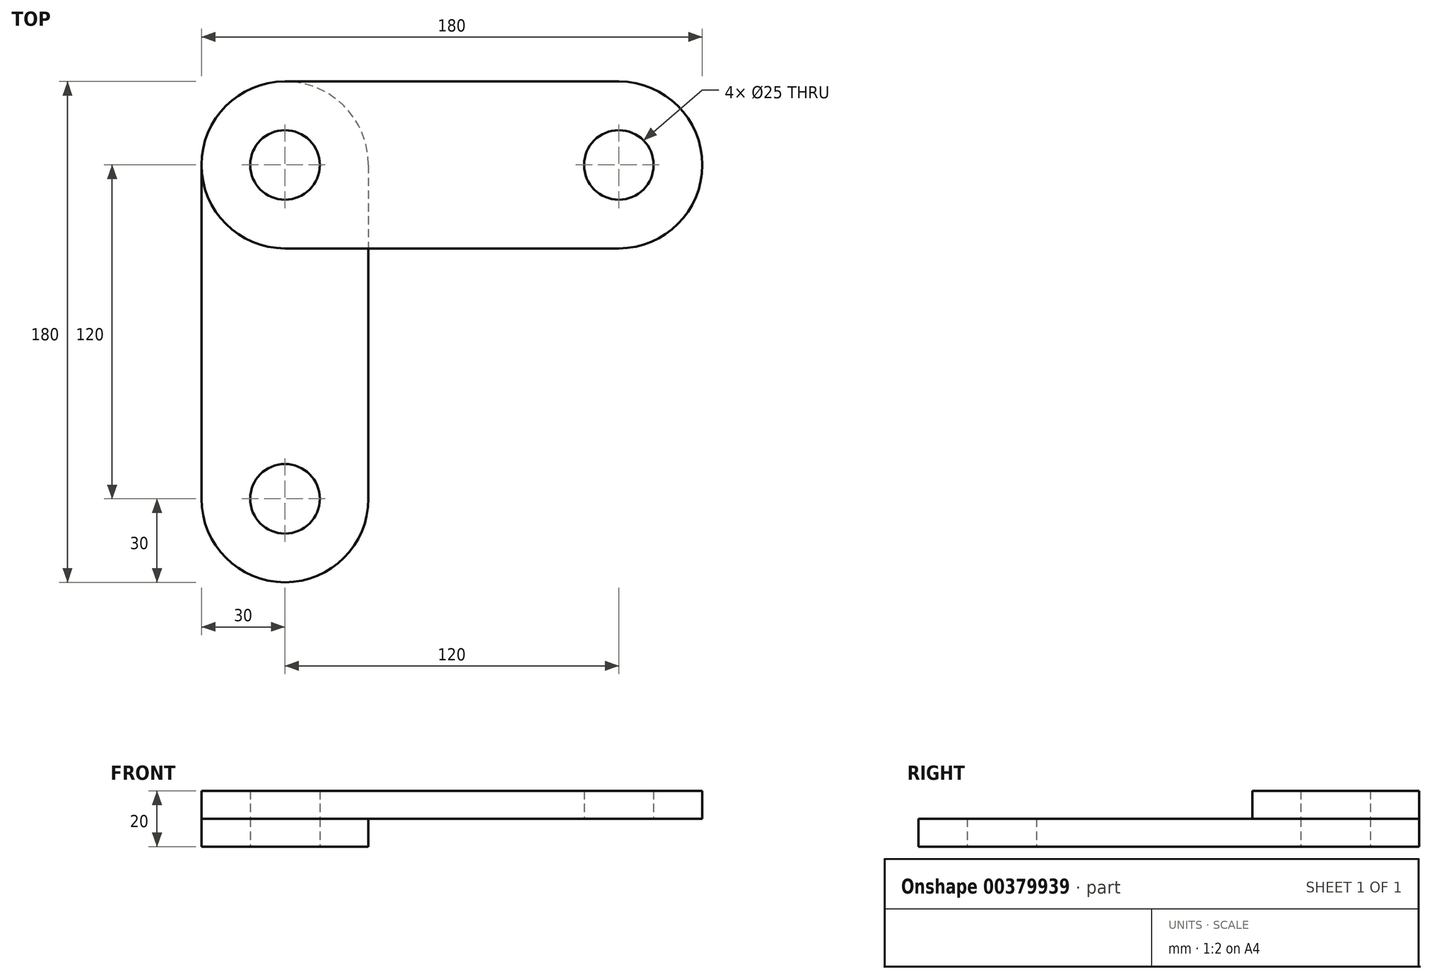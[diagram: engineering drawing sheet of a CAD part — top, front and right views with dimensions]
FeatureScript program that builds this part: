
annotation { "Feature Type Name" : "Feature", "Feature Type Description" : "" }
export const myFeature = defineFeature(function(context is Context, id is Id, definition is map)
    precondition{}
    {
        {
            var Q0;
            Q0=qCreatedBy(makeId("Top.planeOp"),FACE);
            var sketch = newSketch(context, id + "F0", { "sketchPlane" : qUnion([Q0])});
            skCircle(sketch, "E0", {"center": v(0, 0) * mm, "radius": 12.5 * mm});
            skCircle(sketch, "E1", {"center": v(0, 120) * mm, "radius": 12.5 * mm});
            skCircle(sketch, "E2", {"center": v(0, 120) * mm, "radius": 30 * mm});
            skCircle(sketch, "E3", {"center": v(0, 0) * mm, "radius": 30 * mm});
            skLineSegment(sketch, "E4", {"start": v(-30, 0) * mm, "end": v(-30, 120) * mm});
            skLineSegment(sketch, "E5", {"start": v(30, 120) * mm, "end": v(30, 0) * mm});
            skLineSegment(sketch, "E6", {"start": v(0, 120) * mm, "end": v(0, 0) * mm});
            skLineSegment(sketch, "E7", {"start": v(0, 0) * mm, "end": v(-30, 0) * mm, "construction": true});
            skLineSegment(sketch, "E8", {"start": v(0, 120) * mm, "end": v(-30, 120) * mm, "construction": true});
            skSolve(sketch);
        }
        {
            var Q0;
            {var subQ0=sQuery(id+"F0.wireOp",EDGE,"E4");Q0=makeQuery(id+"F0.imprint","IMPRINT",FACE,{"disambiguationData":[TD([[makeQuery(id+"F0.imprint","IMPRINT",EDGE,{"derivedFrom":subQ0}),-1.0]])]});}
            var Q1;
            {var subQ0=sQuery(id+"F0.wireOp",EDGE,"E5");Q1=makeQuery(id+"F0.imprint","IMPRINT",FACE,{"disambiguationData":[TD([[makeQuery(id+"F0.imprint","IMPRINT",EDGE,{"derivedFrom":subQ0}),-1.0]])]});}
            var Q2;
            Q2=makeQuery(id+"F0.imprint","IMPRINT",FACE,{"disambiguationData":[TD([[makeQuery(id+"F0.imprint","IMPRINT",EDGE,{"derivedFrom":sQuery(id+"F0.wireOp",EDGE,"E1")}),-1.0]])]});
            var Q3;
            Q3=makeQuery(id+"F0.imprint","IMPRINT",FACE,{"disambiguationData":[TD([[makeQuery(id+"F0.imprint","IMPRINT",EDGE,{"derivedFrom":sQuery(id+"F0.wireOp",EDGE,"E0")}),-1.0]])]});
            extrude(context, id + "F1", {"entities" : qUnion([Q0, Q1, Q2, Q3]), "depth" : 10 * mm});
        }
        {
            var Q0;
            Q0=makeQuery(id+"F1.opExtrude","SWEPT_BODY",BODY,{"disambiguationData":[OSD([sQuery(id+"F0.wireOp",EDGE,"E0"),sQuery(id+"F0.wireOp",EDGE,"E1"),sQuery(id+"F0.wireOp",EDGE,"E2"),sQuery(id+"F0.wireOp",EDGE,"E3"),sQuery(id+"F0.wireOp",EDGE,"E4"),sQuery(id+"F0.wireOp",EDGE,"E5")])]});
            var Q1;
            Q1=makeQuery(id+"F1.opExtrude","CAP_EDGE",EDGE,{"disambiguationData":[OSD([sQuery(id+"F0.wireOp",EDGE,"E1")])],"isStart":false});
            transform(context, id + "F2", {"entities" : qUnion([Q0]), "transformType" : TransformType.ROTATION, "transformAxis" : qUnion([Q1]), "angle" : 90 * degree, "makeCopy" : true});
        }
        {
            var Q0;
            Q0=makeQuery(id+"F2.opPattern","COPY",BODY,{"derivedFrom":makeQuery(id+"F1.opExtrude","SWEPT_BODY",BODY,{"disambiguationData":[OSD([sQuery(id+"F0.wireOp",EDGE,"E0"),sQuery(id+"F0.wireOp",EDGE,"E1"),sQuery(id+"F0.wireOp",EDGE,"E2"),sQuery(id+"F0.wireOp",EDGE,"E3"),sQuery(id+"F0.wireOp",EDGE,"E4"),sQuery(id+"F0.wireOp",EDGE,"E5")])]}),"instanceName":"1"});
            var Q1;
            Q1=makeQuery(id+"F1.opExtrude","SWEPT_EDGE",EDGE,{"disambiguationData":[OSD([sQuery(id+"F0.wireOp",EDGE,"E2"),sQuery(id+"F0.wireOp",EDGE,"E4")])]});
            transform(context, id + "F3", {"entities" : qUnion([Q0]), "transformType" : TransformType.TRANSLATION_ENTITY, "oppositeDirectionEntity" : true, "transformLine" : qUnion([Q1]), "makeCopy" : false});
        }
    });
